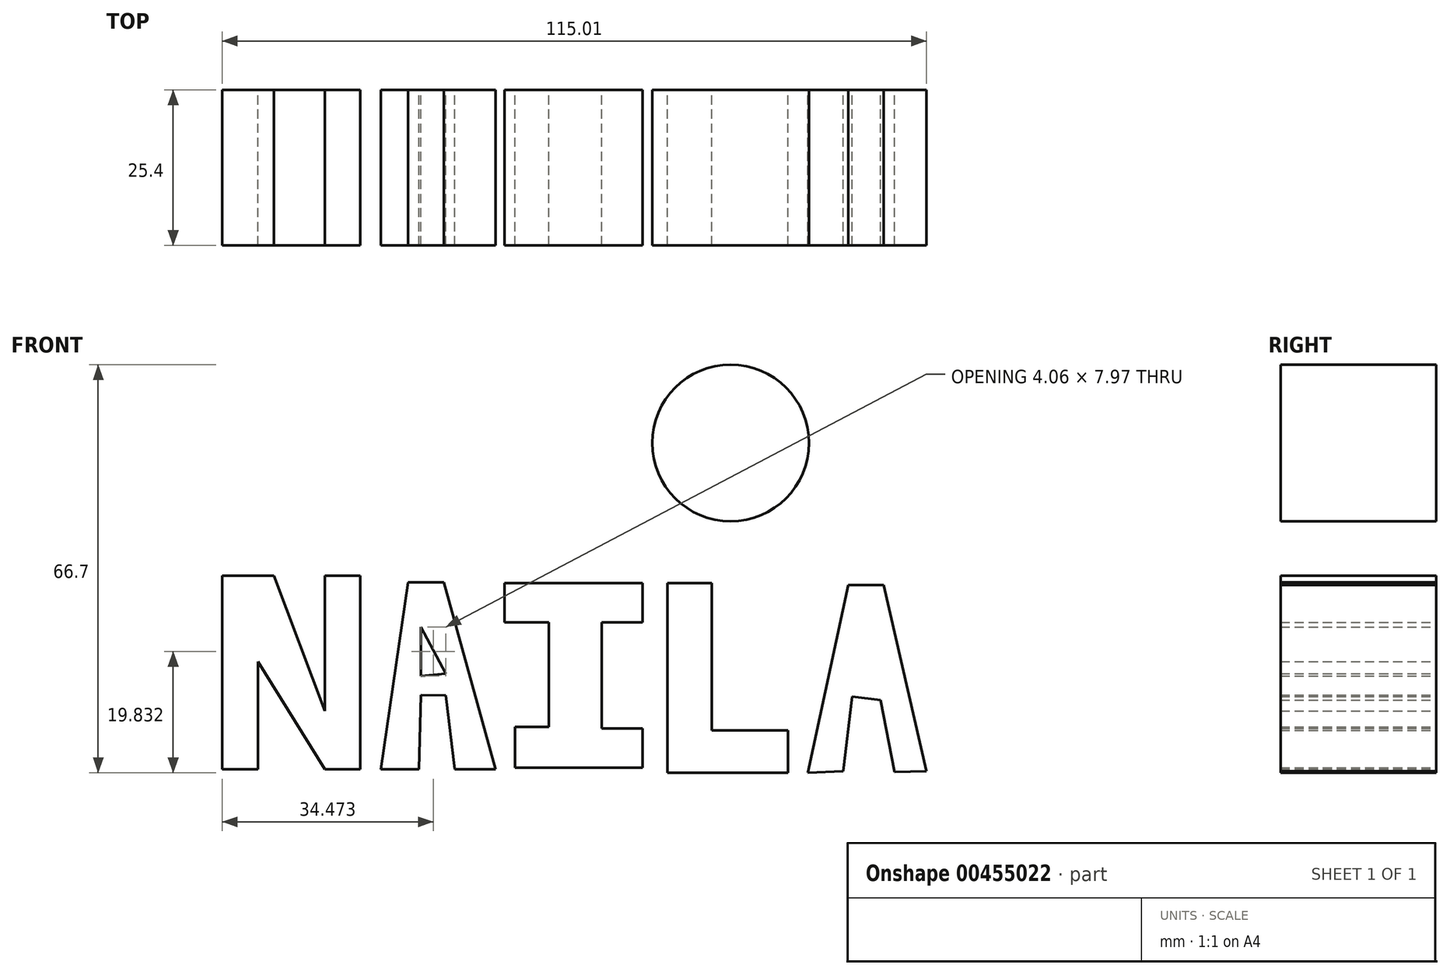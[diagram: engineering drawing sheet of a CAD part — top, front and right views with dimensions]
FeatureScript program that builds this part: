
annotation { "Feature Type Name" : "Feature", "Feature Type Description" : "" }
export const myFeature = defineFeature(function(context is Context, id is Id, definition is map)
    precondition{}
    {
        {
            var Q0;
            Q0=qCreatedBy(makeId("Front.planeOp"),FACE);
            var sketch = newSketch(context, id + "F0", { "sketchPlane" : qUnion([Q0])});
            skLineSegment(sketch, "E0", {"start": v(-104.45, 46.6) * mm, "end": v(-104.45, 14.95) * mm});
            skLineSegment(sketch, "E1", {"start": v(-104.45, 14.95) * mm, "end": v(-104.45, 46.6) * mm});
            skLineSegment(sketch, "E2", {"start": v(-104.45, 14.95) * mm, "end": v(-98.63, 14.95) * mm});
            skLineSegment(sketch, "E3", {"start": v(-98.63, 14.95) * mm, "end": v(-98.63, 32.54) * mm});
            skLineSegment(sketch, "E4", {"start": v(-98.63, 32.54) * mm, "end": v(-87.7, 14.95) * mm});
            skLineSegment(sketch, "E5", {"start": v(-87.7, 24.51) * mm, "end": v(-87.7, 46.6) * mm});
            skLineSegment(sketch, "E6", {"start": v(-81.9, 46.6) * mm, "end": v(-81.9, 14.95) * mm});
            skLineSegment(sketch, "E7", {"start": v(-81.9, 14.95) * mm, "end": v(-87.7, 14.95) * mm});
            skLineSegment(sketch, "E8", {"start": v(-96.03, 46.6) * mm, "end": v(-87.7, 24.51) * mm});
            skLineSegment(sketch, "E9", {"start": v(-104.45, 46.6) * mm, "end": v(-96.03, 46.6) * mm});
            skLineSegment(sketch, "E10", {"start": v(-87.7, 46.6) * mm, "end": v(-81.9, 46.6) * mm});
            skLineSegment(sketch, "E11", {"start": v(-78.54, 14.95) * mm, "end": v(-72.3, 14.95) * mm});
            skLineSegment(sketch, "E12", {"start": v(-66.5, 14.95) * mm, "end": v(-59.84, 14.95) * mm});
            skLineSegment(sketch, "E13", {"start": v(-56.65, 15.24) * mm, "end": v(-35.8, 15.24) * mm});
            skLineSegment(sketch, "E14", {"start": v(-35.8, 15.24) * mm, "end": v(-35.8, 21.62) * mm});
            skLineSegment(sketch, "E15", {"start": v(-56.65, 15.24) * mm, "end": v(-56.65, 21.9) * mm});
            skLineSegment(sketch, "E16", {"start": v(-56.65, 21.9) * mm, "end": v(-51.15, 21.9) * mm});
            skLineSegment(sketch, "E17", {"start": v(-35.8, 21.62) * mm, "end": v(-42.46, 21.62) * mm});
            skLineSegment(sketch, "E18", {"start": v(-42.46, 21.62) * mm, "end": v(-42.46, 39) * mm});
            skLineSegment(sketch, "E19", {"start": v(-51.15, 21.9) * mm, "end": v(-51.15, 39) * mm});
            skLineSegment(sketch, "E20", {"start": v(-51.15, 39) * mm, "end": v(-58.39, 39) * mm});
            skLineSegment(sketch, "E21", {"start": v(-58.39, 39) * mm, "end": v(-58.39, 45.37) * mm});
            skLineSegment(sketch, "E22", {"start": v(-58.39, 45.37) * mm, "end": v(-35.8, 45.37) * mm});
            skLineSegment(sketch, "E23", {"start": v(-35.8, 45.37) * mm, "end": v(-35.8, 39) * mm});
            skLineSegment(sketch, "E24", {"start": v(-35.8, 39) * mm, "end": v(-42.46, 39) * mm});
            skLineSegment(sketch, "E25", {"start": v(-72.3, 14.95) * mm, "end": v(-72, 27.12) * mm});
            skLineSegment(sketch, "E26", {"start": v(-72, 27.12) * mm, "end": v(-67.97, 27.03) * mm});
            skLineSegment(sketch, "E27", {"start": v(-67.97, 27.03) * mm, "end": v(-66.5, 14.95) * mm});
            skLineSegment(sketch, "E28", {"start": v(-78.54, 14.95) * mm, "end": v(-74.1, 45.48) * mm});
            skLineSegment(sketch, "E29", {"start": v(-74.1, 45.48) * mm, "end": v(-68.3, 45.48) * mm});
            skLineSegment(sketch, "E30", {"start": v(-68.3, 45.48) * mm, "end": v(-59.84, 14.95) * mm});
            skLineSegment(sketch, "E31", {"start": v(-31.74, 45.37) * mm, "end": v(-31.74, 14.37) * mm});
            skLineSegment(sketch, "E32", {"start": v(-31.74, 14.37) * mm, "end": v(-12.04, 14.37) * mm});
            skLineSegment(sketch, "E33", {"start": v(-12.04, 14.37) * mm, "end": v(-12.04, 21.33) * mm});
            skLineSegment(sketch, "E34", {"start": v(-12.04, 21.33) * mm, "end": v(-24.5, 21.33) * mm});
            skLineSegment(sketch, "E35", {"start": v(-24.5, 21.33) * mm, "end": v(-24.5, 45.37) * mm});
            skLineSegment(sketch, "E36", {"start": v(-24.5, 45.37) * mm, "end": v(-31.74, 45.37) * mm});
            skLineSegment(sketch, "E37", {"start": v(-8.85, 14.37) * mm, "end": v(-3.05, 14.66) * mm});
            skLineSegment(sketch, "E38", {"start": v(5.36, 14.55) * mm, "end": v(10.56, 14.66) * mm});
            skLineSegment(sketch, "E39", {"start": v(-3.05, 14.66) * mm, "end": v(-1.6, 26.83) * mm});
            skLineSegment(sketch, "E40", {"start": v(-1.6, 26.83) * mm, "end": v(3.07, 26.28) * mm});
            skLineSegment(sketch, "E41", {"start": v(3.07, 26.28) * mm, "end": v(5.36, 14.55) * mm});
            skLineSegment(sketch, "E42", {"start": v(-8.85, 14.37) * mm, "end": v(-2.23, 45.08) * mm});
            skLineSegment(sketch, "E43", {"start": v(-2.23, 45.08) * mm, "end": v(3.57, 45.08) * mm});
            skLineSegment(sketch, "E44", {"start": v(3.57, 45.08) * mm, "end": v(10.56, 14.66) * mm});
            skLineSegment(sketch, "E45", {"start": v(-1.6, 31.47) * mm, "end": v(3.03, 31.47) * mm});
            skLineSegment(sketch, "E46", {"start": v(3.03, 31.47) * mm, "end": v(0.71, 39.58) * mm});
            skLineSegment(sketch, "E47", {"start": v(0.71, 39.58) * mm, "end": v(-1.9, 30.6) * mm});
            skPoint(sketch, "E48.startSnap0", {"position": v(-76.32, 30.22) * mm});
            skLineSegment(sketch, "E49", {"start": v(-67.95, 30.6) * mm, "end": v(-72, 30.22) * mm});
            skLineSegment(sketch, "E50", {"start": v(-72, 30.22) * mm, "end": v(-72, 38.19) * mm});
            skLineSegment(sketch, "E51", {"start": v(-72, 38.19) * mm, "end": v(-67.95, 30.6) * mm});
            skCircle(sketch, "E52", {"center": v(-21.44, 68.28) * mm, "radius": 12.8 * mm});
            skSolve(sketch);
        }
        {
            var Q0;
            Q0 = qSketchRegion(id + "F0", true);
            extrude(context, id + "F1", {"entities" : qUnion([Q0]), "depth" : 25.4 * mm});
        }
    });
